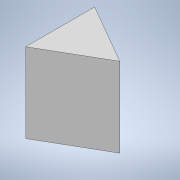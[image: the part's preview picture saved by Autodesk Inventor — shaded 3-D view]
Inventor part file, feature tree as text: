
AUTODESK INVENTOR PART (.ipt)
format: ipt  version: 2020.3 (Build 243373000, 373)  size: 86,528 bytes
history: native  units: mm
features: extrude x1, sketch x1
ambient origin geometry x8: Origin, YZ Plane, XZ Plane, XY Plane, X Axis, Y Axis, Z Axis, Center Point
bodies: Solid1 (feature_tree)
feature tree (2):
  extrude  "Extrusion1"  Depth=32.0mm TaperAngle=0.0deg
  sketch  "Sketch1"  dims[d0=16.0mm d1=32.0mm d2=0.0mm]
